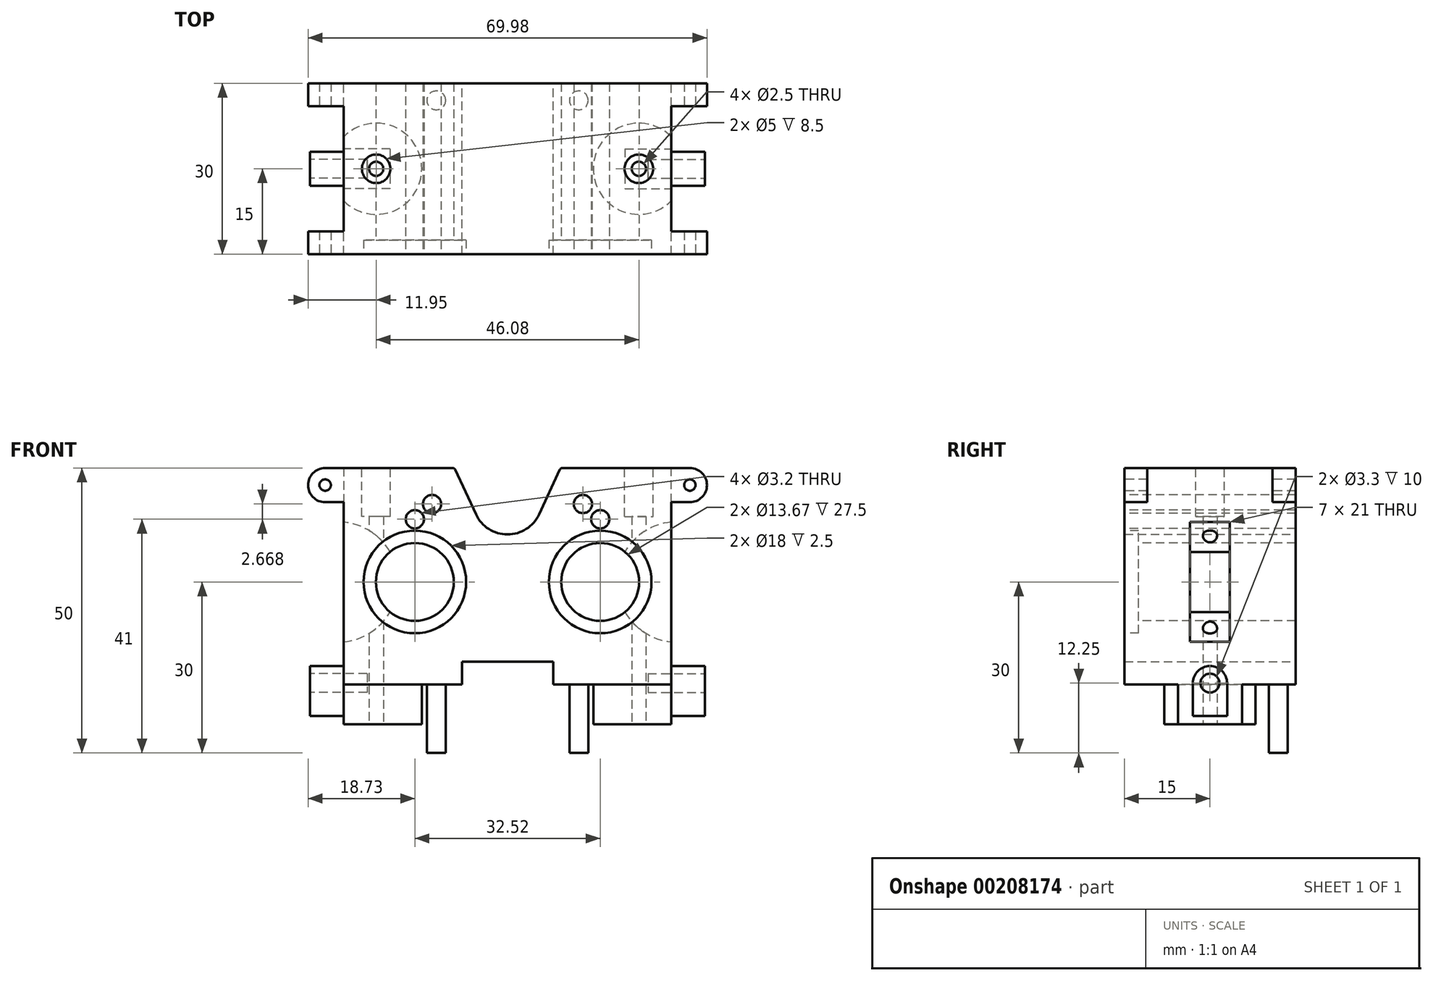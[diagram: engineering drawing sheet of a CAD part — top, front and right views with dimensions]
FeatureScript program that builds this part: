
annotation { "Feature Type Name" : "Feature", "Feature Type Description" : "" }
export const myFeature = defineFeature(function(context is Context, id is Id, definition is map)
    precondition{}
    {
        {
            var Q0;
            Q0=qCreatedBy(makeId("Front.planeOp"),FACE);
            var sketch = newSketch(context, id + "F0", { "sketchPlane" : qUnion([Q0])});
            skCircle(sketch, "E0.3", {"center": v(-13.23, 43.67) * mm, "radius": 1.6 * mm, "construction": true});
            skCircle(sketch, "E0.4", {"center": v(-23.06, 45) * mm, "radius": 1.6 * mm, "construction": true});
            skCircle(sketch, "E0.5", {"center": v(-31.99, 47) * mm, "radius": 1 * mm, "construction": true});
            skLineSegment(sketch, "E0.6", {"start": v(-32, 50) * mm, "end": v(-9.33, 50) * mm});
            skLineSegment(sketch, "E0.7", {"start": v(-5.53, 41.86) * mm, "end": v(-9.33, 50) * mm});
            skArc(sketch, "E0.8", {"start": v(0, 38.33) * mm, "mid": v(-3.28, 39.29) * mm, "end": v(-5.53, 41.86) * mm});
            skArc(sketch, "E0.13", {"start": v(-32, 50) * mm, "mid": v(-34.99, 47) * mm, "end": v(-31.99, 44) * mm});
            skLineSegment(sketch, "E0.14", {"start": v(-31.99, 44) * mm, "end": v(-28.74, 44) * mm});
            skLineSegment(sketch, "E0.17", {"start": v(-28.74, 0) * mm, "end": v(-28.74, 44) * mm});
            skLineSegment(sketch, "E0.18", {"start": v(-28.74, 0) * mm, "end": v(-8, 0) * mm});
            skLineSegment(sketch, "E0.19", {"start": v(-8, 0) * mm, "end": v(-8, 16) * mm});
            skLineSegment(sketch, "E0.20", {"start": v(-8, 16) * mm, "end": v(0, 16) * mm});
            skLineSegment(sketch, "E1", {"start": v(0, 44.43) * mm, "end": v(0, 0) * mm, "construction": true});
            skPoint(sketch, "E2", {"position": v(0, 16) * mm});
            skLineSegment(sketch, "E3", {"start": v(-32, 50) * mm, "end": v(-31.99, 47) * mm, "construction": true});
            skLineSegment(sketch, "E4", {"start": v(-31.99, 47) * mm, "end": v(-31.99, 44) * mm, "construction": true});
            skLineSegment(sketch, "E5", {"start": v(-16.26, 41) * mm, "end": v(-16.26, 30) * mm, "construction": true});
            skCircle(sketch, "E6", {"center": v(-16.26, 30) * mm, "radius": 11 * mm, "construction": true});
            skCircle(sketch, "E7", {"center": v(-16.26, 41) * mm, "radius": 1.6 * mm, "construction": true});
            skLineSegment(sketch, "E8", {"start": v(-16.26, 30) * mm, "end": v(0, 30) * mm, "construction": true});
            skCircle(sketch, "E9.MirrorC", {"center": v(-16.26, 19) * mm, "radius": 1.6 * mm, "construction": true});
            skCircle(sketch, "E10", {"center": v(-20.89, 16.33) * mm, "radius": 1.6 * mm, "construction": true});
            skLineSegment(sketch, "E11", {"start": v(0, 38.33) * mm, "end": v(0, 16) * mm});
            skCircle(sketch, "E12", {"center": v(-16.26, 30) * mm, "radius": 9 * mm, "construction": true});
            skSolve(sketch);
        }
        {
            var Q0;
            Q0=makeQuery(id+"F0.imprint","IMPRINT",FACE,{"disambiguationData":[TD([[makeQuery(id+"F0.imprint","IMPRINT",EDGE,{"derivedFrom":sQuery(id+"F0.wireOp",EDGE,"E0.6")}),-1.0]])]});
            extrude(context, id + "F1", {"entities" : qUnion([Q0]), "depth" : 15 * mm, "hasSecondDirection" : true, "secondDirectionOppositeDirection" : true, "secondDirectionDepth" : 15 * mm});
        }
        {
            var Q0;
            Q0=makeQuery(id+"F1.opExtrude","CAP_FACE",FACE,{"disambiguationData":[OSD([sQuery(id+"F0.wireOp",EDGE,"E0.6"),sQuery(id+"F0.wireOp",EDGE,"E0.7"),sQuery(id+"F0.wireOp",EDGE,"E0.8"),sQuery(id+"F0.wireOp",EDGE,"E0.13"),sQuery(id+"F0.wireOp",EDGE,"E0.14"),sQuery(id+"F0.wireOp",EDGE,"E0.17"),sQuery(id+"F0.wireOp",EDGE,"E0.18"),sQuery(id+"F0.wireOp",EDGE,"E0.19"),sQuery(id+"F0.wireOp",EDGE,"E0.20"),sQuery(id+"F0.wireOp",EDGE,"E11")])],"isStart":false});
            var sketch = newSketch(context, id + "F2", { "sketchPlane" : qUnion([Q0])});
            skPoint(sketch, "E13.0", {"position": v(-16.26, 30) * mm});
            skCircle(sketch, "E14", {"center": v(-16.26, 30) * mm, "radius": 6.83 * mm});
            skCircle(sketch, "E15.0", {"center": v(-13.23, 43.67) * mm, "radius": 1.6 * mm});
            skCircle(sketch, "E15.1", {"center": v(-16.26, 41) * mm, "radius": 1.6 * mm});
            skCircle(sketch, "E16.0", {"center": v(-31.99, 47) * mm, "radius": 1 * mm});
            skSolve(sketch);
        }
        {
            var Q0;
            Q0 = qSketchRegion(id + "F2", true);
            extrude(context, id + "F3", {"entities" : qUnion([Q0]), "operationType" : NewBodyOperationType.REMOVE, "endBound" : BoundingType.THROUGH_ALL, "oppositeDirection" : true, "depth" : 25 * mm});
        }
        {
            var Q0;
            Q0=makeQuery(id+"F1.opExtrude","CAP_FACE",FACE,{"disambiguationData":[OSD([sQuery(id+"F0.wireOp",EDGE,"E0.6"),sQuery(id+"F0.wireOp",EDGE,"E0.7"),sQuery(id+"F0.wireOp",EDGE,"E0.8"),sQuery(id+"F0.wireOp",EDGE,"E0.13"),sQuery(id+"F0.wireOp",EDGE,"E0.14"),sQuery(id+"F0.wireOp",EDGE,"E0.17"),sQuery(id+"F0.wireOp",EDGE,"E0.18"),sQuery(id+"F0.wireOp",EDGE,"E0.19"),sQuery(id+"F0.wireOp",EDGE,"E0.20"),sQuery(id+"F0.wireOp",EDGE,"E11")])],"isStart":false});
            var sketch = newSketch(context, id + "F4", { "sketchPlane" : qUnion([Q0])});
            skCircle(sketch, "E17.0", {"center": v(-16.26, 30) * mm, "radius": 9 * mm});
            skSolve(sketch);
        }
        {
            var Q0;
            Q0=makeQuery(id+"F4.imprint","IMPRINT",FACE,{"disambiguationData":[TD([[makeQuery(id+"F4.imprint","IMPRINT",EDGE,{"derivedFrom":sQuery(id+"F4.wireOp",EDGE,"E17.0")}),1.0]])]});
            extrude(context, id + "F5", {"entities" : qUnion([Q0]), "operationType" : NewBodyOperationType.REMOVE, "oppositeDirection" : true, "depth" : 2.5 * mm});
        }
        {
            var Q0;
            Q0=makeQuery(id+"F1.opExtrude","SWEPT_FACE",FACE,{"disambiguationData":[OSD([sQuery(id+"F0.wireOp",EDGE,"E0.18")])]});
            var sketch = newSketch(context, id + "F6", { "sketchPlane" : qUnion([Q0])});
            skCircle(sketch, "E18", {"center": v(-12.5, 12) * mm, "radius": 1.65 * mm});
            skCircle(sketch, "E19", {"center": v(-23.04, 0) * mm, "radius": 1.25 * mm});
            skArc(sketch, "E20", {"start": v(-28.74, -5.61) * mm, "mid": v(-15.04, 0) * mm, "end": v(-28.74, 5.61) * mm});
            skLineSegment(sketch, "E21", {"start": v(-8, 0) * mm, "end": v(-28.74, 0) * mm, "construction": true});
            skLineSegment(sketch, "E22", {"start": v(-28.74, 5.61) * mm, "end": v(-28.74, -5.61) * mm});
            skCircle(sketch, "E23.MirrorC", {"center": v(-12.5, -12) * mm, "radius": 1.65 * mm});
            skSolve(sketch);
        }
        {
            var Q0;
            Q0=makeQuery(id+"F6.imprint","IMPRINT",FACE,{"disambiguationData":[TD([[makeQuery(id+"F6.imprint","IMPRINT",EDGE,{"derivedFrom":sQuery(id+"F6.wireOp",EDGE,"E19")}),1.0]])]});
            extrude(context, id + "F7", {"entities" : qUnion([Q0]), "operationType" : NewBodyOperationType.REMOVE, "endBound" : BoundingType.THROUGH_ALL, "oppositeDirection" : true, "depth" : 25 * mm});
        }
        {
            var Q0;
            Q0=makeQuery(id+"F6.imprint","IMPRINT",FACE,{"disambiguationData":[TD([[makeQuery(id+"F6.imprint","IMPRINT",EDGE,{"derivedFrom":sQuery(id+"F6.wireOp",EDGE,"E19")}),-1.0]])]});
            extrude(context, id + "F8", {"entities" : qUnion([Q0]), "operationType" : NewBodyOperationType.REMOVE, "oppositeDirection" : true, "depth" : 5 * mm});
        }
        {
            var Q0;
            Q0=makeQuery(id+"F6.imprint","IMPRINT",FACE,{"disambiguationData":[TD([[makeQuery(id+"F6.imprint","IMPRINT",EDGE,{"derivedFrom":sQuery(id+"F6.wireOp",EDGE,"E23.MirrorC")}),-1.0]])]});
            var Q1;
            Q1=makeQuery(id+"F6.imprint","IMPRINT",FACE,{"disambiguationData":[TD([[makeQuery(id+"F6.imprint","IMPRINT",EDGE,{"derivedFrom":sQuery(id+"F6.wireOp",EDGE,"E18")}),1.0]])]});
            extrude(context, id + "F9", {"entities" : qUnion([Q0, Q1]), "operationType" : NewBodyOperationType.REMOVE, "oppositeDirection" : true, "depth" : 12 * mm});
        }
        {
            var Q0;
            Q0=makeQuery(id+"F1.opExtrude","SWEPT_FACE",FACE,{"disambiguationData":[OSD([sQuery(id+"F0.wireOp",EDGE,"E0.17")])]});
            var sketch = newSketch(context, id + "F10", { "sketchPlane" : qUnion([Q0])});
            skArc(sketch, "E24", {"start": v(0, 15.25) * mm, "mid": v(-2.12, 14.37) * mm, "end": v(-3, 12.25) * mm});
            skLineSegment(sketch, "E25", {"start": v(-3, 12.25) * mm, "end": v(-3, 6.5) * mm});
            skLineSegment(sketch, "E26", {"start": v(-3, 6.5) * mm, "end": v(0, 6.5) * mm});
            skLineSegment(sketch, "E27", {"start": v(0, 6.5) * mm, "end": v(0, 15.25) * mm, "construction": true});
            skLineSegment(sketch, "E28.MirrorCS", {"start": v(3, 6.5) * mm, "end": v(0, 6.5) * mm});
            skLineSegment(sketch, "E29.MirrorCS", {"start": v(3, 12.25) * mm, "end": v(3, 6.5) * mm});
            skArc(sketch, "E30.MirrorCS", {"start": v(0, 15.25) * mm, "mid": v(2.12, 14.37) * mm, "end": v(3, 12.25) * mm});
            skCircle(sketch, "E31", {"center": v(0, 12.25) * mm, "radius": 1.65 * mm});
            skLineSegment(sketch, "E32", {"start": v(-3.5, 19.5) * mm, "end": v(0, 19.5) * mm});
            skLineSegment(sketch, "E33", {"start": v(0, 19.5) * mm, "end": v(3.5, 19.5) * mm});
            skLineSegment(sketch, "E34", {"start": v(3.5, 19.5) * mm, "end": v(3.5, 40.5) * mm});
            skLineSegment(sketch, "E35", {"start": v(3.5, 40.5) * mm, "end": v(0, 40.5) * mm});
            skLineSegment(sketch, "E36", {"start": v(0, 40.5) * mm, "end": v(-3.5, 40.5) * mm});
            skLineSegment(sketch, "E37", {"start": v(-3.5, 40.5) * mm, "end": v(-3.5, 19.5) * mm});
            skLineSegment(sketch, "E38", {"start": v(-3.5, 30) * mm, "end": v(3.5, 30) * mm});
            skLineSegment(sketch, "E39", {"start": v(0, 44) * mm, "end": v(11, 44) * mm});
            skLineSegment(sketch, "E40", {"start": v(11, 44) * mm, "end": v(11, 50) * mm});
            skLineSegment(sketch, "E41", {"start": v(11, 50) * mm, "end": v(0, 50) * mm});
            skLineSegment(sketch, "E42", {"start": v(0, 50) * mm, "end": v(-11, 50) * mm});
            skLineSegment(sketch, "E43", {"start": v(-11, 50) * mm, "end": v(-11, 44) * mm});
            skLineSegment(sketch, "E44", {"start": v(-11, 44) * mm, "end": v(0, 44) * mm});
            skSolve(sketch);
        }
        {
            var Q0;
            Q0=makeQuery(id+"F10.imprint","IMPRINT",FACE,{"disambiguationData":[TD([[makeQuery(id+"F10.imprint","IMPRINT",EDGE,{"derivedFrom":sQuery(id+"F10.wireOp",EDGE,"E24")}),1.0]])]});
            var Q1;
            Q1=makeQuery(id+"F10.imprint","IMPRINT",FACE,{"disambiguationData":[TD([[makeQuery(id+"F10.imprint","IMPRINT",EDGE,{"derivedFrom":sQuery(id+"F10.wireOp",EDGE,"E31")}),1.0]])]});
            extrude(context, id + "F11", {"entities" : qUnion([Q0, Q1]), "operationType" : NewBodyOperationType.ADD, "depth" : 5.9 * mm});
        }
        {
            var Q0;
            Q0=makeQuery(id+"F11.opExtrude","CAP_FACE",FACE,{"disambiguationData":[OSD([sQuery(id+"F10.wireOp",EDGE,"E24"),sQuery(id+"F10.wireOp",EDGE,"E25"),sQuery(id+"F10.wireOp",EDGE,"E26"),sQuery(id+"F10.wireOp",EDGE,"E28.MirrorCS"),sQuery(id+"F10.wireOp",EDGE,"E29.MirrorCS"),sQuery(id+"F10.wireOp",EDGE,"E30.MirrorCS")])],"isStart":false});
            var sketch = newSketch(context, id + "F12", { "sketchPlane" : qUnion([Q0])});
            skCircle(sketch, "E45.0", {"center": v(0, 12.25) * mm, "radius": 1.65 * mm});
            skSolve(sketch);
        }
        {
            var Q0;
            Q0=makeQuery(id+"F12.imprint","IMPRINT",FACE,{"disambiguationData":[TD([[makeQuery(id+"F12.imprint","IMPRINT",EDGE,{"derivedFrom":sQuery(id+"F12.wireOp",EDGE,"E45.0")}),1.0]])]});
            var Q1;
            Q1=sQuery(id+"F12.wireOp",EDGE,"E45.0");
            extrude(context, id + "F13", {"entities" : qUnion([Q0]), "operationType" : NewBodyOperationType.REMOVE, "surfaceEntities" : qUnion([Q1]), "oppositeDirection" : true, "depth" : 10 * mm});
        }
        {
            var Q0;
            Q0=qCreatedBy(makeId("Front.planeOp"),FACE);
            var sketch = newSketch(context, id + "F14", { "sketchPlane" : qUnion([Q0])});
            skPoint(sketch, "E46.0", {"position": v(-28.74, 40.5) * mm});
            skPoint(sketch, "E46.1", {"position": v(-28.74, 19.5) * mm});
            skPoint(sketch, "E47", {"position": v(-24.29, 50) * mm});
            skLineSegment(sketch, "E48", {"start": v(-24.29, 50) * mm, "end": v(-24.29, 0) * mm, "construction": true});
            skLineSegment(sketch, "E49", {"start": v(-28.74, 40.5) * mm, "end": v(-28.74, 19.5) * mm, "construction": true});
            skLineSegment(sketch, "E50", {"start": v(-28.74, 30) * mm, "end": v(0, 30) * mm, "construction": true});
            skLineSegment(sketch, "E51", {"start": v(-28.74, 40.5) * mm, "end": v(-28.74, 19.5) * mm});
            skPoint(sketch, "E52", {"position": v(-21.79, 50) * mm});
            skLineSegment(sketch, "E53", {"start": v(-21.79, 50) * mm, "end": v(-21.79, 0) * mm, "construction": true});
            skPoint(sketch, "E54", {"position": v(-24.29, 39) * mm});
            skPoint(sketch, "E55", {"position": v(-24.29, 21) * mm});
            skArc(sketch, "E56", {"start": v(-28.74, 19.5) * mm, "mid": v(-19.2, 30) * mm, "end": v(-28.74, 40.5) * mm});
            skSolve(sketch);
        }
        {
            var Q0;
            Q0=makeQuery(id+"F14.imprint","IMPRINT",FACE,{"disambiguationData":[TD([[makeQuery(id+"F14.imprint","IMPRINT",EDGE,{"derivedFrom":sQuery(id+"F14.wireOp",EDGE,"E51")}),1.0]])]});
            extrude(context, id + "F15", {"entities" : qUnion([Q0]), "operationType" : NewBodyOperationType.REMOVE, "endBound" : BoundingType.SYMMETRIC, "oppositeDirection" : true, "depth" : 7 * mm});
        }
        {
            var Q0;
            Q0=makeQuery(id+"F1.opExtrude","CAP_EDGE",EDGE,{"disambiguationData":[OSD([sQuery(id+"F0.wireOp",EDGE,"E0.13")])],"isStart":true});
            cPoint(context, id + "F16", {"entities" : qUnion([Q0]), "parameter" : 0.5});
        }
        {
            var Q0;
            Q0=qCreatedBy(makeId("Right.planeOp"),FACE);
            var Q1;
            Q1 = qCreatedBy(id + "F16" ,VERTEX);
            cPlane(context, id + "F17", {"entities" : qUnion([Q0, Q1]), "cplaneType" : CPlaneType.PLANE_POINT, "offset" : 25 * mm, "width" : 150 * mm, "height" : 150 * mm});
        }
        {
            var Q0;
            Q0=qCreatedBy(id+"F17.planeOp",FACE);
            var sketch = newSketch(context, id + "F18", { "sketchPlane" : qUnion([Q0])});
            skLineSegment(sketch, "E57.0", {"start": v(0, 44) * mm, "end": v(-11, 44) * mm});
            skLineSegment(sketch, "E57.1", {"start": v(-11, 44) * mm, "end": v(-11, 50) * mm});
            skLineSegment(sketch, "E57.2", {"start": v(-11, 50) * mm, "end": v(0, 50) * mm});
            skLineSegment(sketch, "E57.3", {"start": v(0, 50) * mm, "end": v(11, 50) * mm});
            skLineSegment(sketch, "E57.4", {"start": v(11, 50) * mm, "end": v(11, 44) * mm});
            skLineSegment(sketch, "E57.5", {"start": v(11, 44) * mm, "end": v(0, 44) * mm});
            skSolve(sketch);
        }
        {
            var Q0;
            Q0=makeQuery(id+"F18.imprint","IMPRINT",FACE,{"disambiguationData":[TD([[makeQuery(id+"F18.imprint","IMPRINT",EDGE,{"derivedFrom":sQuery(id+"F18.wireOp",EDGE,"E57.0")}),-1.0]])]});
            var Q1;
            Q1=makeQuery(id+"F1.opExtrude","SWEPT_FACE",FACE,{"disambiguationData":[OSD([sQuery(id+"F0.wireOp",EDGE,"E0.17")])]});
            extrude(context, id + "F19", {"entities" : qUnion([Q0]), "operationType" : NewBodyOperationType.REMOVE, "endBound" : BoundingType.UP_TO_SURFACE, "endBoundEntityFace" : qUnion([Q1]), "depth" : 25 * mm});
        }
        {
            var Q0;
            Q0=makeQuery(id+"F1.opExtrude","SWEPT_EDGE",EDGE,{"disambiguationData":[OSD([sQuery(id+"F0.wireOp",EDGE,"E0.6"),sQuery(id+"F0.wireOp",EDGE,"E0.7")])]});
            var Q1;
            Q1=makeQuery(id+"F23.opPattern","COPY",EDGE,{"derivedFrom":makeQuery(id+"F1.opExtrude","SWEPT_EDGE",EDGE,{"disambiguationData":[OSD([sQuery(id+"F0.wireOp",EDGE,"E0.6"),sQuery(id+"F0.wireOp",EDGE,"E0.7")])]}),"instanceName":"1"});
            var Q2;
            {var subQ0=sQuery(id+"F6.wireOp",EDGE,"E22");var subQ1=sQuery(id+"F6.wireOp",EDGE,"E20");var subQ2=sQuery(id+"F0.wireOp",EDGE,"E0.18");var subQ3=sQuery(id+"F0.wireOp",EDGE,"E0.17");Q2=makeQuery(id+"F23.opPattern","COPY",EDGE,{"derivedFrom":makeQuery(id+"F8.boolean.opBoolean","COPY",EDGE,{"derivedFrom":makeQuery(id+"F8.opExtrude","SWEPT_EDGE",EDGE,{"disambiguationData":[OSD([subQ3,subQ2,subQ1,subQ0]),TDD([makeQuery(id+"F6.imprint","INTERSECT",VERTEX,{"disambiguationData":[OD(0.0)],"derivedFrom":[makeQuery(id+"F1.opExtrude","SWEPT_EDGE",EDGE,{"disambiguationData":[OSD([subQ3,subQ2])]}),subQ1,subQ0]})])]})}),"instanceName":"1"});}
            var Q3;
            {var subQ0=sQuery(id+"F6.wireOp",EDGE,"E22");var subQ1=sQuery(id+"F6.wireOp",EDGE,"E20");var subQ2=sQuery(id+"F0.wireOp",EDGE,"E0.18");var subQ3=sQuery(id+"F0.wireOp",EDGE,"E0.17");Q3=makeQuery(id+"F23.opPattern","COPY",EDGE,{"derivedFrom":makeQuery(id+"F8.boolean.opBoolean","COPY",EDGE,{"derivedFrom":makeQuery(id+"F8.opExtrude","SWEPT_EDGE",EDGE,{"disambiguationData":[OSD([subQ3,subQ2,subQ1,subQ0]),TDD([makeQuery(id+"F6.imprint","INTERSECT",VERTEX,{"disambiguationData":[OD(1.0)],"derivedFrom":[makeQuery(id+"F1.opExtrude","SWEPT_EDGE",EDGE,{"disambiguationData":[OSD([subQ3,subQ2])]}),subQ1,subQ0]})])]})}),"instanceName":"1"});}
            var Q4;
            {var subQ0=sQuery(id+"F6.wireOp",EDGE,"E22");var subQ1=sQuery(id+"F6.wireOp",EDGE,"E20");var subQ2=sQuery(id+"F0.wireOp",EDGE,"E0.18");var subQ3=sQuery(id+"F0.wireOp",EDGE,"E0.17");Q4=makeQuery(id+"F8.boolean.opBoolean","COPY",EDGE,{"derivedFrom":makeQuery(id+"F8.opExtrude","SWEPT_EDGE",EDGE,{"disambiguationData":[OSD([subQ3,subQ2,subQ1,subQ0]),TDD([makeQuery(id+"F6.imprint","INTERSECT",VERTEX,{"disambiguationData":[OD(1.0)],"derivedFrom":[makeQuery(id+"F1.opExtrude","SWEPT_EDGE",EDGE,{"disambiguationData":[OSD([subQ3,subQ2])]}),subQ1,subQ0]})])]})});}
            var Q5;
            {var subQ0=sQuery(id+"F6.wireOp",EDGE,"E22");var subQ1=sQuery(id+"F6.wireOp",EDGE,"E20");var subQ2=sQuery(id+"F0.wireOp",EDGE,"E0.18");var subQ3=sQuery(id+"F0.wireOp",EDGE,"E0.17");Q5=makeQuery(id+"F8.boolean.opBoolean","COPY",EDGE,{"derivedFrom":makeQuery(id+"F8.opExtrude","SWEPT_EDGE",EDGE,{"disambiguationData":[OSD([subQ3,subQ2,subQ1,subQ0]),TDD([makeQuery(id+"F6.imprint","INTERSECT",VERTEX,{"disambiguationData":[OD(0.0)],"derivedFrom":[makeQuery(id+"F1.opExtrude","SWEPT_EDGE",EDGE,{"disambiguationData":[OSD([subQ3,subQ2])]}),subQ1,subQ0]})])]})});}
            fillet(context, id + "F20", {"entities" : qUnion([Q0, Q1, Q2, Q3, Q4, Q5]), "radius" : 0.5 * mm, "tangentPropagation" : true, "allowEdgeOverflow" : false});
        }
        {
            var Q0;
            Q0=makeQuery(id+"F1.opExtrude","SWEPT_FACE",FACE,{"disambiguationData":[OSD([sQuery(id+"F0.wireOp",EDGE,"E0.6")])]});
            var sketch = newSketch(context, id + "F21", { "sketchPlane" : qUnion([Q0])});
            skCircle(sketch, "E58", {"center": v(-23.04, 0) * mm, "radius": 2.5 * mm});
            skSolve(sketch);
        }
        {
            var Q0;
            Q0=makeQuery(id+"F21.imprint","IMPRINT",FACE,{"disambiguationData":[TD([[makeQuery(id+"F21.imprint","IMPRINT",EDGE,{"derivedFrom":sQuery(id+"F21.wireOp",EDGE,"E58")}),1.0]])]});
            extrude(context, id + "F22", {"entities" : qUnion([Q0]), "operationType" : NewBodyOperationType.REMOVE, "oppositeDirection" : true, "depth" : 8.5 * mm});
        }
        {
            var Q0;
            Q0=makeQuery(id+"F1.opExtrude","SWEPT_BODY",BODY,{"disambiguationData":[OSD([sQuery(id+"F0.wireOp",EDGE,"E0.6"),sQuery(id+"F0.wireOp",EDGE,"E0.7"),sQuery(id+"F0.wireOp",EDGE,"E0.8"),sQuery(id+"F0.wireOp",EDGE,"E0.13"),sQuery(id+"F0.wireOp",EDGE,"E0.14"),sQuery(id+"F0.wireOp",EDGE,"E0.17"),sQuery(id+"F0.wireOp",EDGE,"E0.18"),sQuery(id+"F0.wireOp",EDGE,"E0.19"),sQuery(id+"F0.wireOp",EDGE,"E0.20"),sQuery(id+"F0.wireOp",EDGE,"E11")])]});
            var Q1;
            Q1=qCreatedBy(makeId("Right.planeOp"),FACE);
            mirror(context, id + "F23", {"operationType" : NewBodyOperationType.ADD, "entities" : qUnion([Q0]), "mirrorPlane" : qUnion([Q1])});
        }
    });
